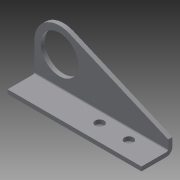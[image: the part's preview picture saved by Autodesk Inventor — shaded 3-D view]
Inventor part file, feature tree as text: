
AUTODESK INVENTOR PART (.ipt)
format: ipt  version: 2013 (Build 170138000, 138)  size: 192,000 bytes
history: native  units: in
note: dims shown in document units (in); Inventor stores cm internally (conversion verified against a paired STEP export)
features: other x7, sheet_metal_op x6, sketch x5, reference x2
ambient origin geometry x8: Origin, YZ Plane, XZ Plane, XY Plane, X Axis, Y Axis, Z Axis, Center Point
feature tree (20):
  sheet_metal_op  "Face2"
  sheet_metal_op  "Flange2"
  sheet_metal_op  "Face3"
  sketch  "Sketch1"  dims[d2=4.0in]
  other  "Plate2"
  sketch  "Sketch5"  dims[d5=0.266in]
  other  "Plate4"
  sheet_metal_op  "Bend2"
  sheet_metal_op  "Corner2"
  sketch  "Sketch6"  dims[d7=0.266in]
  sketch  "Sketch8"  dims[d9=1.5in]
  other  "Plate5"
  sheet_metal_op  "Bend3"
  sketch  "Sketch9"  dims[d18=0.125in d19=0.125in d40=0.125in d41=0.0625in d42=0.25in d43=0.125in d44=1.75in d45=90.0deg d46=0.05in d47=0.5in d48=0.125in d49=0.125in d50=1.125in d51=0.75in d52=0.75in d53=0.25in d54=0.125in d55=0.0in d57=0.75in d58=0.25in d59=0.25in d60=1.0in d61=0.125in d62=0.125in d63=0.0625in d64=0.25in d65=0.125in d66=0.125in d67=0.0in d0=0.832in d1=0.125in d3=0.25in d4=0.125in d6=0.0625in d8=0.125in d10=0.0in]
  reference  "Reference2"
  reference  "Reference3"
  other  "Cut3"
  other  "Cut4"
  other  "Definition1"
  other  "Cut1"
